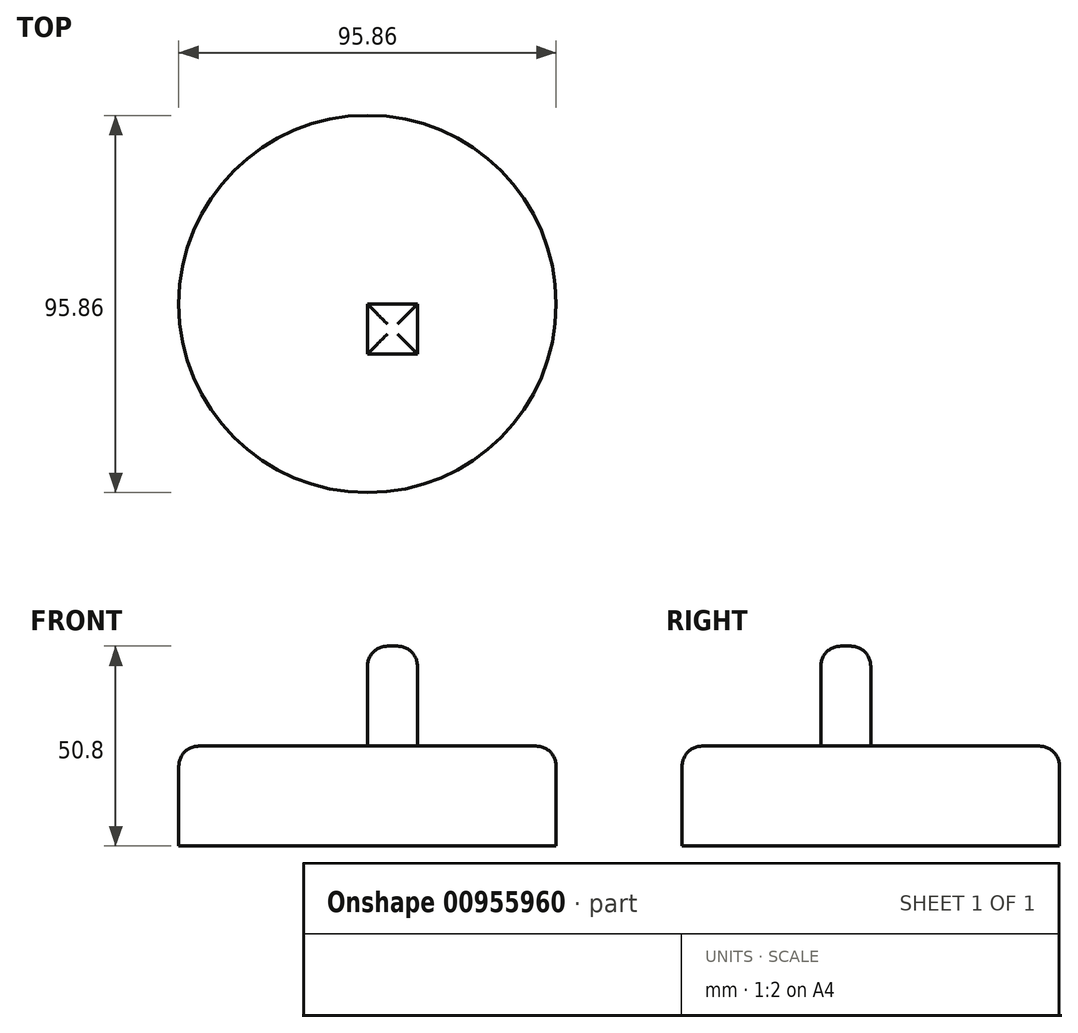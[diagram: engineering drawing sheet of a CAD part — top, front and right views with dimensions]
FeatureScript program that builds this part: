
annotation { "Feature Type Name" : "Feature", "Feature Type Description" : "" }
export const myFeature = defineFeature(function(context is Context, id is Id, definition is map)
    precondition{}
    {
        {
            var Q0;
            Q0=qCreatedBy(makeId("Top.planeOp"),FACE);
            var sketch = newSketch(context, id + "F0", { "sketchPlane" : qUnion([Q0])});
            skCircle(sketch, "E0", {"center": v(0, 0) * mm, "radius": 47.93 * mm});
            skSolve(sketch);
        }
        {
            var Q0;
            Q0=makeQuery(id+"F0.imprint","IMPRINT",FACE,{"disambiguationData":[TD([[makeQuery(id+"F0.imprint","IMPRINT",EDGE,{"derivedFrom":sQuery(id+"F0.wireOp",EDGE,"E0")}),1.0]])]});
            extrude(context, id + "F1", {"entities" : qUnion([Q0]), "depth" : 25.4 * mm, "offsetDistance" : 25.4 * mm});
        }
        {
            var Q0;
            Q0=makeQuery(id+"F1.opExtrude","CAP_FACE",FACE,{"disambiguationData":[OSD([sQuery(id+"F0.wireOp",EDGE,"E0")])],"isStart":false});
            var sketch = newSketch(context, id + "F2", { "sketchPlane" : qUnion([Q0])});
            skLineSegment(sketch, "E1.bottom", {"start": v(0, 0) * mm, "end": v(12.7, 0) * mm});
            skLineSegment(sketch, "E1.top", {"start": v(0, -12.7) * mm, "end": v(12.7, -12.7) * mm});
            skLineSegment(sketch, "E1.left", {"start": v(0, 0) * mm, "end": v(0, -12.7) * mm});
            skLineSegment(sketch, "E1.right", {"start": v(12.7, 0) * mm, "end": v(12.7, -12.7) * mm});
            skSolve(sketch);
        }
        {
            var Q0;
            Q0=makeQuery(id+"F2.imprint","IMPRINT",FACE,{"disambiguationData":[TD([[makeQuery(id+"F2.imprint","IMPRINT",EDGE,{"derivedFrom":sQuery(id+"F2.wireOp",EDGE,"E1.bottom")}),-1.0]])]});
            extrude(context, id + "F3", {"entities" : qUnion([Q0]), "operationType" : NewBodyOperationType.ADD, "depth" : 25.4 * mm, "offsetDistance" : 25.4 * mm});
        }
        {
            var Q0;
            Q0=makeQuery(id+"F1.opExtrude","CAP_EDGE",EDGE,{"disambiguationData":[OSD([sQuery(id+"F0.wireOp",EDGE,"E0")])],"isStart":false});
            var Q1;
            Q1=makeQuery(id+"F3.opExtrude","CAP_EDGE",EDGE,{"disambiguationData":[OSD([sQuery(id+"F2.wireOp",EDGE,"E1.top")])],"isStart":false});
            var Q2;
            Q2=makeQuery(id+"F3.opExtrude","CAP_EDGE",EDGE,{"disambiguationData":[OSD([sQuery(id+"F2.wireOp",EDGE,"E1.right")])],"isStart":false});
            var Q3;
            Q3=makeQuery(id+"F3.opExtrude","CAP_EDGE",EDGE,{"disambiguationData":[OSD([sQuery(id+"F2.wireOp",EDGE,"E1.bottom")])],"isStart":false});
            var Q4;
            Q4=makeQuery(id+"F3.opExtrude","CAP_EDGE",EDGE,{"disambiguationData":[OSD([sQuery(id+"F2.wireOp",EDGE,"E1.left")])],"isStart":false});
            fillet(context, id + "F4", {"entities" : qUnion([Q0, Q1, Q2, Q3, Q4]), "radius" : 5.08 * mm, "tangentPropagation" : true, "allowEdgeOverflow" : false});
        }
    });
